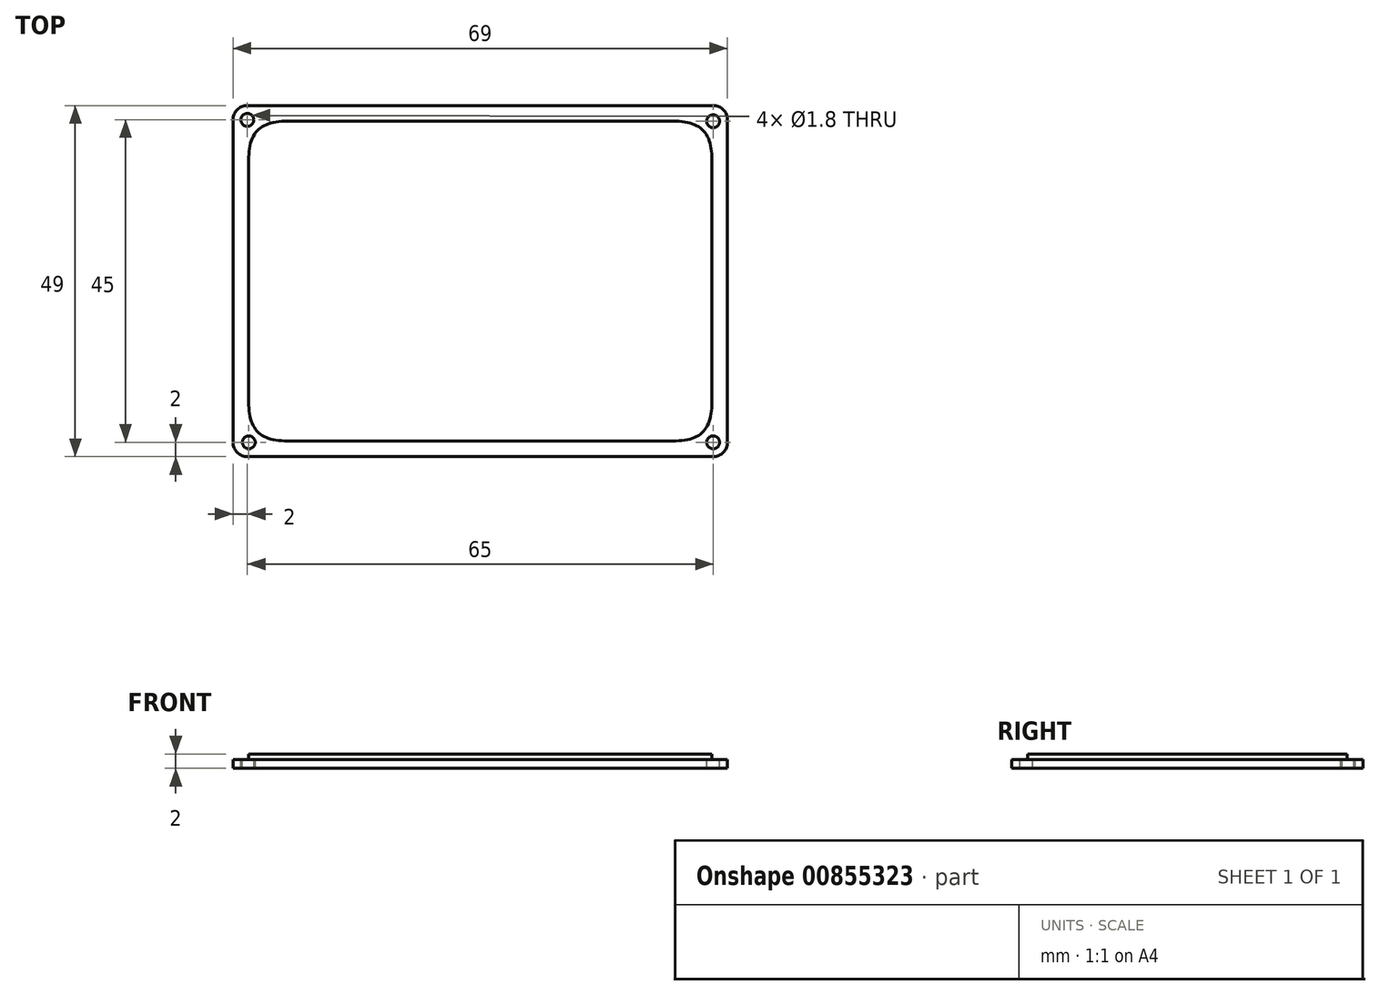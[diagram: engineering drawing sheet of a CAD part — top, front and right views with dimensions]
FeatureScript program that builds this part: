
annotation { "Feature Type Name" : "Feature", "Feature Type Description" : "" }
export const myFeature = defineFeature(function(context is Context, id is Id, definition is map)
    precondition{}
    {
        {
            var Q0;
            Q0=qCreatedBy(makeId("Top.planeOp"),FACE);
            var sketch = newSketch(context, id + "F0", { "sketchPlane" : qUnion([Q0])});
            skLineSegment(sketch, "E0.bottom", {"start": v(-34.5, 24.5) * mm, "end": v(34.5, 24.5) * mm});
            skLineSegment(sketch, "E0.top", {"start": v(-34.5, -24.5) * mm, "end": v(34.5, -24.5) * mm});
            skLineSegment(sketch, "E0.left", {"start": v(-34.5, 24.5) * mm, "end": v(-34.5, -24.5) * mm});
            skLineSegment(sketch, "E0.right", {"start": v(34.5, 24.5) * mm, "end": v(34.5, -24.5) * mm});
            skPoint(sketch, "E0.middle", {"position": v(0, 0) * mm});
            skLineSegment(sketch, "E1", {"start": v(-32.3, 22.3) * mm, "end": v(32.3, 22.3) * mm});
            skLineSegment(sketch, "E2", {"start": v(32.3, 22.3) * mm, "end": v(32.3, -22.3) * mm});
            skLineSegment(sketch, "E3", {"start": v(32.3, -22.3) * mm, "end": v(-32.3, -22.3) * mm});
            skLineSegment(sketch, "E4", {"start": v(-32.3, -22.3) * mm, "end": v(-32.3, 22.3) * mm});
            skSolve(sketch);
        }
        {
            var Q0;
            Q0=makeQuery(id+"F0.imprint","IMPRINT",FACE,{"disambiguationData":[TD([[makeQuery(id+"F0.imprint","IMPRINT",EDGE,{"derivedFrom":sQuery(id+"F0.wireOp",EDGE,"E1")}),-1.0]])]});
            extrude(context, id + "F1", {"entities" : qUnion([Q0]), "depth" : 2 * mm, "offsetDistance" : 25 * mm});
        }
        {
            var Q0;
            Q0 = qSketchRegion(id + "F0", true);
            extrude(context, id + "F2", {"entities" : qUnion([Q0]), "operationType" : NewBodyOperationType.ADD, "depth" : 1.2 * mm, "offsetDistance" : 25 * mm});
        }
        {
            var Q0;
            Q0=makeQuery(id+"F1.opExtrude","SWEPT_EDGE",EDGE,{"disambiguationData":[OSD([sQuery(id+"F0.wireOp",EDGE,"E3"),sQuery(id+"F0.wireOp",EDGE,"E4")])]});
            var Q1;
            Q1=makeQuery(id+"F1.opExtrude","SWEPT_EDGE",EDGE,{"disambiguationData":[OSD([sQuery(id+"F0.wireOp",EDGE,"E2"),sQuery(id+"F0.wireOp",EDGE,"E3")])]});
            var Q2;
            Q2=makeQuery(id+"F1.opExtrude","SWEPT_EDGE",EDGE,{"disambiguationData":[OSD([sQuery(id+"F0.wireOp",EDGE,"E1"),sQuery(id+"F0.wireOp",EDGE,"E2")])]});
            var Q3;
            Q3=makeQuery(id+"F1.opExtrude","SWEPT_EDGE",EDGE,{"disambiguationData":[OSD([sQuery(id+"F0.wireOp",EDGE,"E1"),sQuery(id+"F0.wireOp",EDGE,"E4")])]});
            fillet(context, id + "F3", {"entities" : qUnion([Q0, Q1, Q2, Q3]), "radius" : 5 * mm, "tangentPropagation" : true, "rho" : 0.5, "crossSection" : FilletCrossSection.CONIC, "allowEdgeOverflow" : false});
        }
        {
            var Q0;
            Q0=makeQuery(id+"F2.opExtrude","SWEPT_EDGE",EDGE,{"disambiguationData":[OSD([sQuery(id+"F0.wireOp",EDGE,"E0.bottom"),sQuery(id+"F0.wireOp",EDGE,"E0.left")])]});
            var Q1;
            Q1=makeQuery(id+"F2.opExtrude","SWEPT_EDGE",EDGE,{"disambiguationData":[OSD([sQuery(id+"F0.wireOp",EDGE,"E0.top"),sQuery(id+"F0.wireOp",EDGE,"E0.left")])]});
            var Q2;
            Q2=makeQuery(id+"F2.opExtrude","SWEPT_EDGE",EDGE,{"disambiguationData":[OSD([sQuery(id+"F0.wireOp",EDGE,"E0.bottom"),sQuery(id+"F0.wireOp",EDGE,"E0.right")])]});
            var Q3;
            Q3=makeQuery(id+"F2.opExtrude","SWEPT_EDGE",EDGE,{"disambiguationData":[OSD([sQuery(id+"F0.wireOp",EDGE,"E0.top"),sQuery(id+"F0.wireOp",EDGE,"E0.right")])]});
            fillet(context, id + "F4", {"entities" : qUnion([Q0, Q1, Q2, Q3]), "radius" : 2 * mm, "tangentPropagation" : true, "allowEdgeOverflow" : false});
        }
        {
            var Q0;
            Q0=makeQuery(id+"F2.opExtrude","CAP_FACE",FACE,{"disambiguationData":[OSD([sQuery(id+"F0.wireOp",EDGE,"E0.bottom"),sQuery(id+"F0.wireOp",EDGE,"E0.top"),sQuery(id+"F0.wireOp",EDGE,"E0.left"),sQuery(id+"F0.wireOp",EDGE,"E0.right"),sQuery(id+"F0.wireOp",EDGE,"E1"),sQuery(id+"F0.wireOp",EDGE,"E2"),sQuery(id+"F0.wireOp",EDGE,"E3"),sQuery(id+"F0.wireOp",EDGE,"E4")])],"isStart":false});
            var sketch = newSketch(context, id + "F5", { "sketchPlane" : qUnion([Q0])});
            skPoint(sketch, "E5", {"position": v(-32.5, 22.5) * mm});
            skPoint(sketch, "E6", {"position": v(-32.3, -22.5) * mm});
            skPoint(sketch, "E7", {"position": v(32.5, -22.5) * mm});
            skPoint(sketch, "E8", {"position": v(32.5, 22.3) * mm});
            skSolve(sketch);
        }
        {
            var Q0;
            Q0=sQuery(id+"F5.wireOp",VERTEX,"E6");
            var Q1;
            Q1=sQuery(id+"F5.wireOp",VERTEX,"E5");
            var Q2;
            Q2=sQuery(id+"F5.wireOp",VERTEX,"E7");
            var Q3;
            Q3=sQuery(id+"F5.wireOp",VERTEX,"E8");
            var Q4;
            Q4=makeQuery(id+"F1.opExtrude","SWEPT_BODY",BODY,{"disambiguationData":[OSD([sQuery(id+"F0.wireOp",EDGE,"E1"),sQuery(id+"F0.wireOp",EDGE,"E2"),sQuery(id+"F0.wireOp",EDGE,"E3"),sQuery(id+"F0.wireOp",EDGE,"E4")])]});
            hole(context, id + "F6", {"style" : HoleStyle.SIMPLE, "endStyle" : HoleEndStyle.BLIND, "holeDiameter" : 1.8 * mm, "majorDiameter" : 5 * mm, "holeDepth" : 6 * mm, "isTappedThrough" : true, "tappedDepth" : 12 * mm, "tapClearance" : 3, "locations" : qUnion([Q0, Q1, Q2, Q3]), "scope" : qUnion([Q4])});
        }
        {
            var Q0;
            {var subQ0=sQuery(id+"F0.wireOp",EDGE,"E4");var subQ1=sQuery(id+"F0.wireOp",EDGE,"E3");var subQ2=sQuery(id+"F0.wireOp",EDGE,"E2");var subQ3=sQuery(id+"F0.wireOp",EDGE,"E1");Q0=makeQuery(id+"F2.boolean.opBoolean","MERGE",FACE,{"derivedFrom":[makeQuery(id+"F1.opExtrude","CAP_FACE",FACE,{"disambiguationData":[OSD([subQ3,subQ2,subQ1,subQ0])],"isStart":true}),makeQuery(id+"F2.opExtrude","CAP_FACE",FACE,{"disambiguationData":[OSD([sQuery(id+"F0.wireOp",EDGE,"E0.bottom"),sQuery(id+"F0.wireOp",EDGE,"E0.top"),sQuery(id+"F0.wireOp",EDGE,"E0.left"),sQuery(id+"F0.wireOp",EDGE,"E0.right"),subQ3,subQ2,subQ1,subQ0])],"isStart":true})]});}
            var sketch = newSketch(context, id + "F7", { "sketchPlane" : qUnion([Q0])});
            skText(sketch, "E9", { "text": "TIM", "fontName": "OpenSans-Regular.ttf"});
            const initialGuessF7  = {"E9": [-0.02772, -0.00926, 1, 0, 0.02327]};
            skSetInitialGuess(sketch, initialGuessF7);
            skSolve(sketch);
        }
        {
            var Q0;
            Q0 = qConstructionFilter(qBodyType(qCreatedBy(id + "F7" ,EDGE), BodyType.WIRE), ConstructionObject.NO);
            extrude(context, id + "F8", {"bodyType" : ToolBodyType.SURFACE, "surfaceEntities" : qUnion([Q0]), "oppositeDirection" : true, "depth" : 0.3 * mm, "offsetDistance" : 25 * mm});
        }
    });
